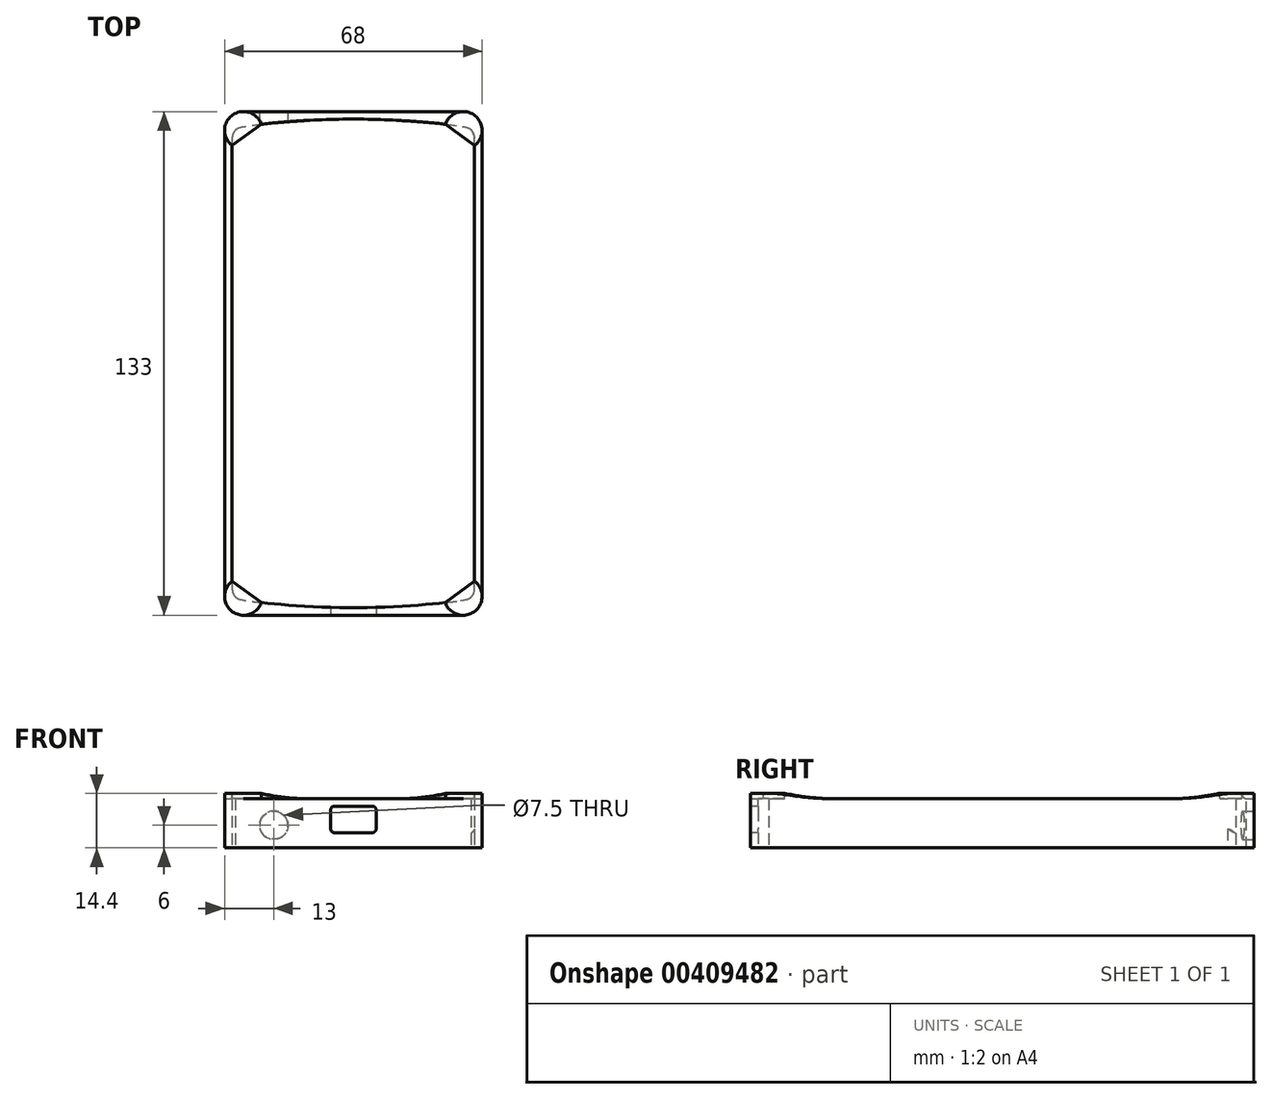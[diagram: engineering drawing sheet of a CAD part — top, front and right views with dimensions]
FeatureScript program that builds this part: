
annotation { "Feature Type Name" : "Feature", "Feature Type Description" : "" }
export const myFeature = defineFeature(function(context is Context, id is Id, definition is map)
    precondition{}
    {
        {
            var Q0;
            Q0=qCreatedBy(makeId("Top.planeOp"),FACE);
            var sketch = newSketch(context, id + "F0", { "sketchPlane" : qUnion([Q0])});
            skPoint(sketch, "E0.visualSharp", {"position": v(0, 127) * mm});
            skPoint(sketch, "E1.visualSharp", {"position": v(64, 127) * mm});
            skArc(sketch, "E1.filletArc", {"start": v(64, 124) * mm, "mid": v(63.77, 125.15) * mm, "end": v(63.12, 126.12) * mm});
            skFitSpline(sketch, "E2", {"points": [v(0, 124) * mm, v(0.88, 126.12) * mm, v(3, 127) * mm, v(32, 129) * mm, v(61, 127) * mm, v(63.12, 126.12) * mm, v(64, 124) * mm], "startDerivative": vector(8.1, 27.14) * mm, "endDerivative": vector(8.1, -27.14) * mm});
            skArc(sketch, "E3.trimOffspring", {"start": v(0.88, 126.12) * mm, "mid": v(0.23, 125.15) * mm, "end": v(0, 124) * mm});
            skArc(sketch, "E4.MirrorCS", {"start": v(0.88, 2.88) * mm, "mid": v(0.23, 3.85) * mm, "end": v(0, 5) * mm});
            skPoint(sketch, "E5.MirrorP", {"position": v(64, 2) * mm});
            skFitSpline(sketch, "E6.MirrorCS", {"points": [v(0, 5) * mm, v(0.88, 2.88) * mm, v(3, 2) * mm, v(32, 0) * mm, v(61, 2) * mm, v(63.12, 2.88) * mm, v(64, 5) * mm], "startDerivative": vector(8.1, -27.14) * mm, "endDerivative": vector(8.1, 27.14) * mm});
            skArc(sketch, "E7.MirrorCS", {"start": v(63.12, 2.88) * mm, "mid": v(63.77, 3.85) * mm, "end": v(64, 5) * mm});
            skLineSegment(sketch, "E8", {"start": v(0, 124) * mm, "end": v(0, 5) * mm});
            skLineSegment(sketch, "E9", {"start": v(64, 5) * mm, "end": v(64, 124) * mm});
            skLineSegment(sketch, "E10", {"start": v(3, -2) * mm, "end": v(61, -2) * mm});
            skLineSegment(sketch, "E11", {"start": v(66, 3) * mm, "end": v(66, 126) * mm});
            skLineSegment(sketch, "E12", {"start": v(61, 131) * mm, "end": v(3, 131) * mm});
            skLineSegment(sketch, "E13", {"start": v(-2, 126) * mm, "end": v(-2, 3) * mm});
            skPoint(sketch, "E14.orphan", {"position": v(-4.29, -2) * mm});
            skPoint(sketch, "E15.visualSharp", {"position": v(-2, 131) * mm});
            skArc(sketch, "E15.filletArc", {"start": v(3, 131) * mm, "mid": v(-0.54, 129.54) * mm, "end": v(-2, 126) * mm});
            skPoint(sketch, "E16.visualSharp", {"position": v(66, 131) * mm});
            skArc(sketch, "E16.filletArc", {"start": v(66, 126) * mm, "mid": v(64.54, 129.54) * mm, "end": v(61, 131) * mm});
            skPoint(sketch, "E17.visualSharp", {"position": v(66, -2) * mm});
            skArc(sketch, "E17.filletArc", {"start": v(61, -2) * mm, "mid": v(64.54, -0.54) * mm, "end": v(66, 3) * mm});
            skPoint(sketch, "E18.visualSharp", {"position": v(-2, -2) * mm});
            skArc(sketch, "E18.filletArc", {"start": v(-2, 3) * mm, "mid": v(-0.54, -0.54) * mm, "end": v(3, -2) * mm});
            skPoint(sketch, "E19", {"position": v(32, 120) * mm});
            skPoint(sketch, "E20.visualSharp", {"position": v(40, 108.5) * mm});
            skArc(sketch, "E21.MirrorCS", {"start": v(36.93, 13) * mm, "mid": v(36.22, 13.3) * mm, "end": v(35.93, 14) * mm});
            skArc(sketch, "E22.MirrorCS", {"start": v(35.93, 21.5) * mm, "mid": v(36.22, 22.2) * mm, "end": v(36.93, 22.5) * mm});
            skLineSegment(sketch, "E23.MirrorCS", {"start": v(20, 115.5) * mm, "end": v(24.8, 115.5) * mm});
            skLineSegment(sketch, "E24.MirrorCS", {"start": v(20, 108.5) * mm, "end": v(21.5, 108.5) * mm});
            skArc(sketch, "E25.MirrorCS", {"start": v(49.93, 14) * mm, "mid": v(49.64, 13.3) * mm, "end": v(48.93, 13) * mm});
            skArc(sketch, "E26.MirrorCS", {"start": v(48.93, 22.5) * mm, "mid": v(49.64, 22.2) * mm, "end": v(49.93, 21.5) * mm});
            skArc(sketch, "E27.MirrorCS", {"start": v(21.5, 108.5) * mm, "mid": v(23.27, 107.77) * mm, "end": v(24, 106) * mm});
            skLineSegment(sketch, "E28.MirrorCS", {"start": v(36.93, 13) * mm, "end": v(48.93, 13) * mm});
            skPoint(sketch, "E29.MirrorP", {"position": v(35.93, 22.5) * mm});
            skLineSegment(sketch, "E30.MirrorCS", {"start": v(49.93, 14) * mm, "end": v(49.93, 21.5) * mm});
            skPoint(sketch, "E31.MirrorP", {"position": v(35.93, 13) * mm});
            skLineSegment(sketch, "E32.MirrorCS", {"start": v(48.93, 22.5) * mm, "end": v(36.93, 22.5) * mm});
            skLineSegment(sketch, "E33.MirrorCS", {"start": v(35.93, 21.5) * mm, "end": v(35.93, 14) * mm});
            skLineSegment(sketch, "E34.MirrorCS", {"start": v(24, 82) * mm, "end": v(24, 106) * mm});
            skPoint(sketch, "E35.MirrorP", {"position": v(24, 108.5) * mm});
            skArc(sketch, "E36.MirrorCS", {"start": v(20, 108.5) * mm, "mid": v(16.5, 112) * mm, "end": v(20, 115.5) * mm});
            skArc(sketch, "E37.MirrorCS", {"start": v(40, 82) * mm, "mid": v(32, 74) * mm, "end": v(24, 82) * mm});
            skArc(sketch, "E38.MirrorCS", {"start": v(24.8, 115.5) * mm, "mid": v(33.8, 119.8) * mm, "end": v(40, 112) * mm});
            skLineSegment(sketch, "E39", {"start": v(40, 82) * mm, "end": v(40, 112) * mm});
            skSolve(sketch);
        }
        {
            var Q0;
            Q0=makeQuery(id+"F0.imprint","IMPRINT",FACE,{"disambiguationData":[TD([[makeQuery(id+"F0.imprint","IMPRINT",EDGE,{"derivedFrom":sQuery(id+"F0.wireOp",EDGE,"E1.filletArc")}),-1.0]])]});
            var Q1;
            Q1=makeQuery(id+"F0.imprint","IMPRINT",FACE,{"disambiguationData":[TD([[makeQuery(id+"F0.imprint","IMPRINT",EDGE,{"derivedFrom":sQuery(id+"F0.wireOp",EDGE,"E1.filletArc")}),1.0]])]});
            extrude(context, id + "F1", {"entities" : qUnion([Q0, Q1]), "depth" : 5 * mm});
        }
        {
            var Q0;
            Q0=makeQuery(id+"F1.opExtrude","SWEPT_FACE",FACE,{"disambiguationData":[OSD([sQuery(id+"F0.wireOp",EDGE,"E10")])]});
            var sketch = newSketch(context, id + "F2", { "sketchPlane" : qUnion([Q0])});
            skLineSegment(sketch, "E40", {"start": v(64, 5) * mm, "end": v(0, 5) * mm});
            skPoint(sketch, "E41", {"position": v(32, 0) * mm});
            skFitSpline(sketch, "E42", {"points": [v(0, 5) * mm, v(1.5, 3.5) * mm, v(32, 2) * mm, v(62.5, 3.5) * mm, v(64, 5) * mm], "startDerivative": vector(7.84, -15.51) * mm, "endDerivative": vector(7.84, 15.51) * mm});
            skSolve(sketch);
        }
        {
            var Q0;
            Q0 = qSketchRegion(id + "F2", true);
            extrude(context, id + "F3", {"entities" : qUnion([Q0]), "operationType" : NewBodyOperationType.REMOVE, "oppositeDirection" : true, "depth" : 134 * mm});
        }
        {
            var Q0;
            Q0 = qSketchRegion(id + "F0", true);
            extrude(context, id + "F4", {"entities" : qUnion([Q0]), "operationType" : NewBodyOperationType.ADD, "depth" : 13 * mm});
        }
        {
            var Q0;
            {var subQ0=sQuery(id+"F0.wireOp",EDGE,"E10");Q0=makeQuery(id+"F4.boolean.opBoolean","MERGE",FACE,{"derivedFrom":[makeQuery(id+"F1.opExtrude","SWEPT_FACE",FACE,{"disambiguationData":[OSD([subQ0])]}),makeQuery(id+"F4.opExtrude","SWEPT_FACE",FACE,{"disambiguationData":[OSD([subQ0])]})]});}
            var sketch = newSketch(context, id + "F5", { "sketchPlane" : qUnion([Q0])});
            skLineSegment(sketch, "E43", {"start": v(37, 4) * mm, "end": v(27, 4) * mm});
            skLineSegment(sketch, "E44", {"start": v(38, 5) * mm, "end": v(38, 10) * mm});
            skLineSegment(sketch, "E45", {"start": v(27, 11) * mm, "end": v(37, 11) * mm});
            skLineSegment(sketch, "E46", {"start": v(26, 10) * mm, "end": v(26, 5) * mm});
            skPoint(sketch, "E47.visualSharp", {"position": v(26, 11) * mm});
            skArc(sketch, "E47.filletArc", {"start": v(27, 11) * mm, "mid": v(26.3, 10.7) * mm, "end": v(26, 10) * mm});
            skPoint(sketch, "E48.visualSharp", {"position": v(38, 11) * mm});
            skArc(sketch, "E48.filletArc", {"start": v(38, 10) * mm, "mid": v(37.7, 10.7) * mm, "end": v(37, 11) * mm});
            skPoint(sketch, "E49.visualSharp", {"position": v(38, 4) * mm});
            skArc(sketch, "E49.filletArc", {"start": v(37, 4) * mm, "mid": v(37.7, 4.3) * mm, "end": v(38, 5) * mm});
            skPoint(sketch, "E50.visualSharp", {"position": v(26, 4) * mm});
            skArc(sketch, "E50.filletArc", {"start": v(26, 5) * mm, "mid": v(26.3, 4.3) * mm, "end": v(27, 4) * mm});
            skPoint(sketch, "E51", {"position": v(32, 7.5) * mm});
            skSolve(sketch);
        }
        {
            var Q0;
            Q0 = qSketchRegion(id + "F5", true);
            extrude(context, id + "F6", {"entities" : qUnion([Q0]), "operationType" : NewBodyOperationType.REMOVE, "oppositeDirection" : true, "depth" : 3 * mm});
        }
        {
            var Q0;
            Q0=makeQuery(id+"F4.opExtrude","CAP_FACE",FACE,{"disambiguationData":[OSD([sQuery(id+"F0.wireOp",EDGE,"E1.filletArc"),sQuery(id+"F0.wireOp",EDGE,"E2"),sQuery(id+"F0.wireOp",EDGE,"E3.trimOffspring"),sQuery(id+"F0.wireOp",EDGE,"E4.MirrorCS"),sQuery(id+"F0.wireOp",EDGE,"E6.MirrorCS"),sQuery(id+"F0.wireOp",EDGE,"E7.MirrorCS"),sQuery(id+"F0.wireOp",EDGE,"E8"),sQuery(id+"F0.wireOp",EDGE,"E9"),sQuery(id+"F0.wireOp",EDGE,"E10"),sQuery(id+"F0.wireOp",EDGE,"E11"),sQuery(id+"F0.wireOp",EDGE,"E12"),sQuery(id+"F0.wireOp",EDGE,"E13"),sQuery(id+"F0.wireOp",EDGE,"E15.filletArc"),sQuery(id+"F0.wireOp",EDGE,"E16.filletArc"),sQuery(id+"F0.wireOp",EDGE,"E17.filletArc"),sQuery(id+"F0.wireOp",EDGE,"E18.filletArc")])],"isStart":false});
            var sketch = newSketch(context, id + "F7", { "sketchPlane" : qUnion([Q0])});
            skArc(sketch, "E52", {"start": v(56.28, 1.35) * mm, "mid": v(63.95, -1.04) * mm, "end": v(64, 7) * mm});
            skLineSegment(sketch, "E53", {"start": v(64, 7) * mm, "end": v(56.28, 1.35) * mm});
            skArc(sketch, "E54", {"start": v(0, 7) * mm, "mid": v(0.05, -1.04) * mm, "end": v(7.72, 1.35) * mm});
            skLineSegment(sketch, "E55", {"start": v(7.72, 1.35) * mm, "end": v(0, 7) * mm});
            skArc(sketch, "E56", {"start": v(7.72, 127.65) * mm, "mid": v(0.05, 130.04) * mm, "end": v(0, 122) * mm});
            skArc(sketch, "E57", {"start": v(64, 122) * mm, "mid": v(63.95, 130.04) * mm, "end": v(56.28, 127.65) * mm});
            skLineSegment(sketch, "E58", {"start": v(7.72, 127.65) * mm, "end": v(0, 122) * mm});
            skLineSegment(sketch, "E59", {"start": v(64, 122) * mm, "end": v(56.28, 127.65) * mm});
            skSolve(sketch);
        }
        {
            var Q0;
            Q0 = qSketchRegion(id + "F7", true);
            extrude(context, id + "F8", {"entities" : qUnion([Q0]), "operationType" : NewBodyOperationType.ADD, "depth" : 1.4 * mm});
        }
        {
            var Q0;
            {var subQ2=sQuery(id+"F0.wireOp",EDGE,"E10");var subQ4=sQuery(id+"F7.wireOp",EDGE,"E52");Q0=makeQuery(id+"F8.boolean.opBoolean","SPLIT",EDGE,{"disambiguationData":[TD([makeQuery(id+"F1.opExtrude","SWEPT_FACE",FACE,{"disambiguationData":[OSD([subQ2])]})])],"derivedFrom":makeQuery(id+"F8.opExtrude","CAP_EDGE",EDGE,{"disambiguationData":[OSD([subQ4])],"isStart":true})});}
            var Q1;
            {var subQ3=sQuery(id+"F0.wireOp",EDGE,"E10");var subQ4=sQuery(id+"F7.wireOp",EDGE,"E54");Q1=makeQuery(id+"F8.boolean.opBoolean","SPLIT",EDGE,{"disambiguationData":[TD([makeQuery(id+"F1.opExtrude","SWEPT_FACE",FACE,{"disambiguationData":[OSD([subQ3])]})])],"derivedFrom":makeQuery(id+"F8.opExtrude","CAP_EDGE",EDGE,{"disambiguationData":[OSD([subQ4])],"isStart":true})});}
            var Q2;
            {var subQ2=sQuery(id+"F0.wireOp",EDGE,"E13");var subQ4=sQuery(id+"F7.wireOp",EDGE,"E54");Q2=makeQuery(id+"F8.boolean.opBoolean","SPLIT",EDGE,{"disambiguationData":[TD([makeQuery(id+"F1.opExtrude","SWEPT_FACE",FACE,{"disambiguationData":[OSD([subQ2])]})])],"derivedFrom":makeQuery(id+"F8.opExtrude","CAP_EDGE",EDGE,{"disambiguationData":[OSD([subQ4])],"isStart":true})});}
            var Q3;
            {var subQ3=sQuery(id+"F7.wireOp",EDGE,"E56");var subQ4=sQuery(id+"F0.wireOp",EDGE,"E13");Q3=makeQuery(id+"F8.boolean.opBoolean","SPLIT",EDGE,{"disambiguationData":[TD([makeQuery(id+"F1.opExtrude","SWEPT_FACE",FACE,{"disambiguationData":[OSD([subQ4])]})])],"derivedFrom":makeQuery(id+"F8.opExtrude","CAP_EDGE",EDGE,{"disambiguationData":[OSD([subQ3])],"isStart":true})});}
            var Q4;
            {var subQ3=sQuery(id+"F0.wireOp",EDGE,"E12");var subQ4=sQuery(id+"F7.wireOp",EDGE,"E57");Q4=makeQuery(id+"F8.boolean.opBoolean","SPLIT",EDGE,{"disambiguationData":[TD([makeQuery(id+"F1.opExtrude","SWEPT_FACE",FACE,{"disambiguationData":[OSD([subQ3])]})])],"derivedFrom":makeQuery(id+"F8.opExtrude","CAP_EDGE",EDGE,{"disambiguationData":[OSD([subQ4])],"isStart":true})});}
            var Q5;
            {var subQ2=sQuery(id+"F0.wireOp",EDGE,"E12");var subQ4=sQuery(id+"F7.wireOp",EDGE,"E56");Q5=makeQuery(id+"F8.boolean.opBoolean","SPLIT",EDGE,{"disambiguationData":[TD([makeQuery(id+"F1.opExtrude","SWEPT_FACE",FACE,{"disambiguationData":[OSD([subQ2])]})])],"derivedFrom":makeQuery(id+"F8.opExtrude","CAP_EDGE",EDGE,{"disambiguationData":[OSD([subQ4])],"isStart":true})});}
            var Q6;
            {var subQ2=sQuery(id+"F0.wireOp",EDGE,"E11");var subQ4=sQuery(id+"F7.wireOp",EDGE,"E57");Q6=makeQuery(id+"F8.boolean.opBoolean","SPLIT",EDGE,{"disambiguationData":[TD([makeQuery(id+"F1.opExtrude","SWEPT_FACE",FACE,{"disambiguationData":[OSD([subQ2])]})])],"derivedFrom":makeQuery(id+"F8.opExtrude","CAP_EDGE",EDGE,{"disambiguationData":[OSD([subQ4])],"isStart":true})});}
            var Q7;
            {var subQ2=sQuery(id+"F0.wireOp",EDGE,"E11");var subQ4=sQuery(id+"F7.wireOp",EDGE,"E52");Q7=makeQuery(id+"F8.boolean.opBoolean","SPLIT",EDGE,{"disambiguationData":[TD([makeQuery(id+"F1.opExtrude","SWEPT_FACE",FACE,{"disambiguationData":[OSD([subQ2])]})])],"derivedFrom":makeQuery(id+"F8.opExtrude","CAP_EDGE",EDGE,{"disambiguationData":[OSD([subQ4])],"isStart":true})});}
            fillet(context, id + "F9", {"entities" : qUnion([Q0, Q1, Q2, Q3, Q4, Q5, Q6, Q7]), "radius" : 50 * mm, "tangentPropagation" : true, "allowEdgeOverflow" : false});
        }
        {
            var Q0;
            {var subQ0=sQuery(id+"F0.wireOp",EDGE,"E12");Q0=makeQuery(id+"F4.boolean.opBoolean","MERGE",FACE,{"derivedFrom":[makeQuery(id+"F1.opExtrude","SWEPT_FACE",FACE,{"disambiguationData":[OSD([subQ0])]}),makeQuery(id+"F4.opExtrude","SWEPT_FACE",FACE,{"disambiguationData":[OSD([subQ0])]})]});}
            var sketch = newSketch(context, id + "F10", { "sketchPlane" : qUnion([Q0])});
            skCircle(sketch, "E60", {"center": v(-11, 6) * mm, "radius": 3.75 * mm});
            skSolve(sketch);
        }
        {
            var Q0;
            Q0 = qSketchRegion(id + "F10", true);
            extrude(context, id + "F11", {"entities" : qUnion([Q0]), "operationType" : NewBodyOperationType.REMOVE, "oppositeDirection" : true, "depth" : 5 * mm});
        }
    });
